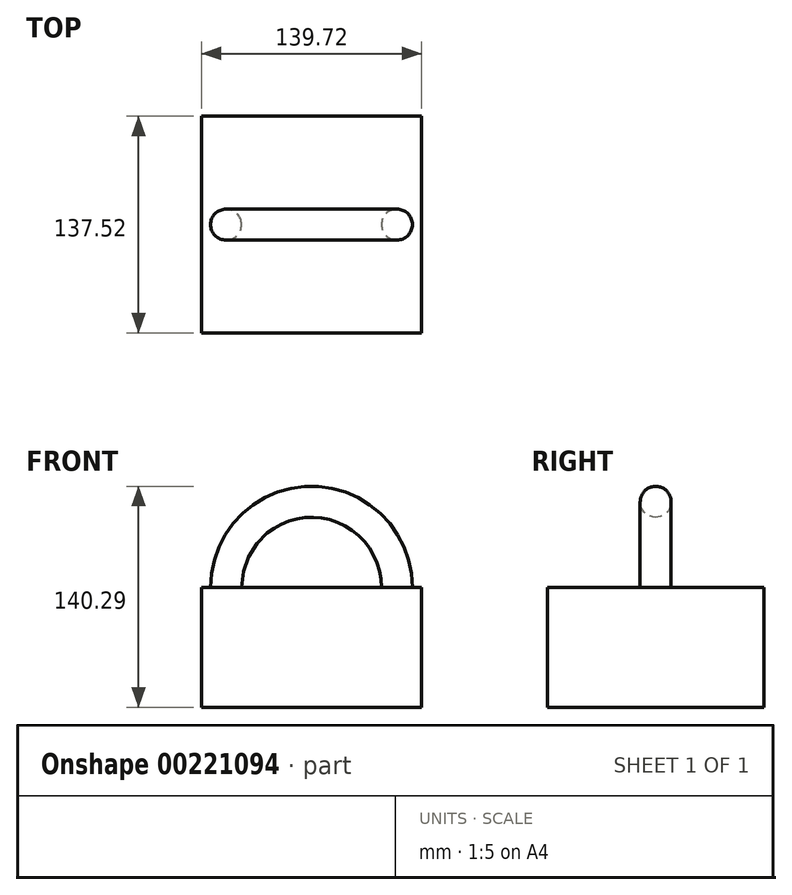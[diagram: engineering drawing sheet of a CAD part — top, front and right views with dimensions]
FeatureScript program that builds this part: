
annotation { "Feature Type Name" : "Feature", "Feature Type Description" : "" }
export const myFeature = defineFeature(function(context is Context, id is Id, definition is map)
    precondition{}
    {
        {
            var Q0;
            Q0=qCreatedBy(makeId("Top.planeOp"),FACE);
            var sketch = newSketch(context, id + "F0", { "sketchPlane" : qUnion([Q0])});
            skLineSegment(sketch, "E0.bottom", {"start": v(69.86, -68.76) * mm, "end": v(-69.86, -68.76) * mm});
            skLineSegment(sketch, "E0.top", {"start": v(69.86, 68.76) * mm, "end": v(-69.86, 68.76) * mm});
            skLineSegment(sketch, "E0.left", {"start": v(69.86, -68.76) * mm, "end": v(69.86, 68.76) * mm});
            skLineSegment(sketch, "E0.right", {"start": v(-69.86, -68.76) * mm, "end": v(-69.86, 68.76) * mm});
            skPoint(sketch, "E0.middle", {"position": v(0, 0) * mm});
            skLineSegment(sketch, "E1", {"start": v(0, 68.76) * mm, "end": v(0, -68.76) * mm});
            skSolve(sketch);
        }
        {
            var Q0;
            Q0=qCreatedBy(makeId("Top.planeOp"),FACE);
            var sketch = newSketch(context, id + "F1", { "sketchPlane" : qUnion([Q0])});
            skCircle(sketch, "E2", {"center": v(54.26, 0) * mm, "radius": 9.82 * mm});
            skSolve(sketch);
        }
        {
            var Q0;
            {var subQ0=sQuery(id+"F0.wireOp",EDGE,"E0.right");Q0=makeQuery(id+"F0.imprint","IMPRINT",FACE,{"disambiguationData":[TD([[makeQuery(id+"F0.imprint","IMPRINT",EDGE,{"derivedFrom":subQ0}),-1.0]])]});}
            extrude(context, id + "F2", {"entities" : qUnion([Q0]), "oppositeDirection" : true, "depth" : 76.2 * mm});
        }
        {
            var Q0;
            {var subQ0=sQuery(id+"F0.wireOp",EDGE,"E0.left");Q0=makeQuery(id+"F0.imprint","IMPRINT",FACE,{"disambiguationData":[TD([[makeQuery(id+"F0.imprint","IMPRINT",EDGE,{"derivedFrom":subQ0}),1.0]])]});}
            extrude(context, id + "F3", {"entities" : qUnion([Q0]), "operationType" : NewBodyOperationType.ADD, "oppositeDirection" : true, "depth" : 76.2 * mm});
        }
        {
            var Q0;
            Q0=makeQuery(id+"F1.imprint","IMPRINT",FACE,{"disambiguationData":[TD([[makeQuery(id+"F1.imprint","IMPRINT",EDGE,{"derivedFrom":sQuery(id+"F1.wireOp",EDGE,"E2")}),1.0]])]});
            var Q1;
            Q1=sQuery(id+"F0.wireOp",EDGE,"E1");
            revolve(context, id + "F4", {"operationType" : NewBodyOperationType.ADD, "entities" : qUnion([Q0]), "axis" : qUnion([Q1]), "revolveType" : RevolveType.FULL});
        }
    });
